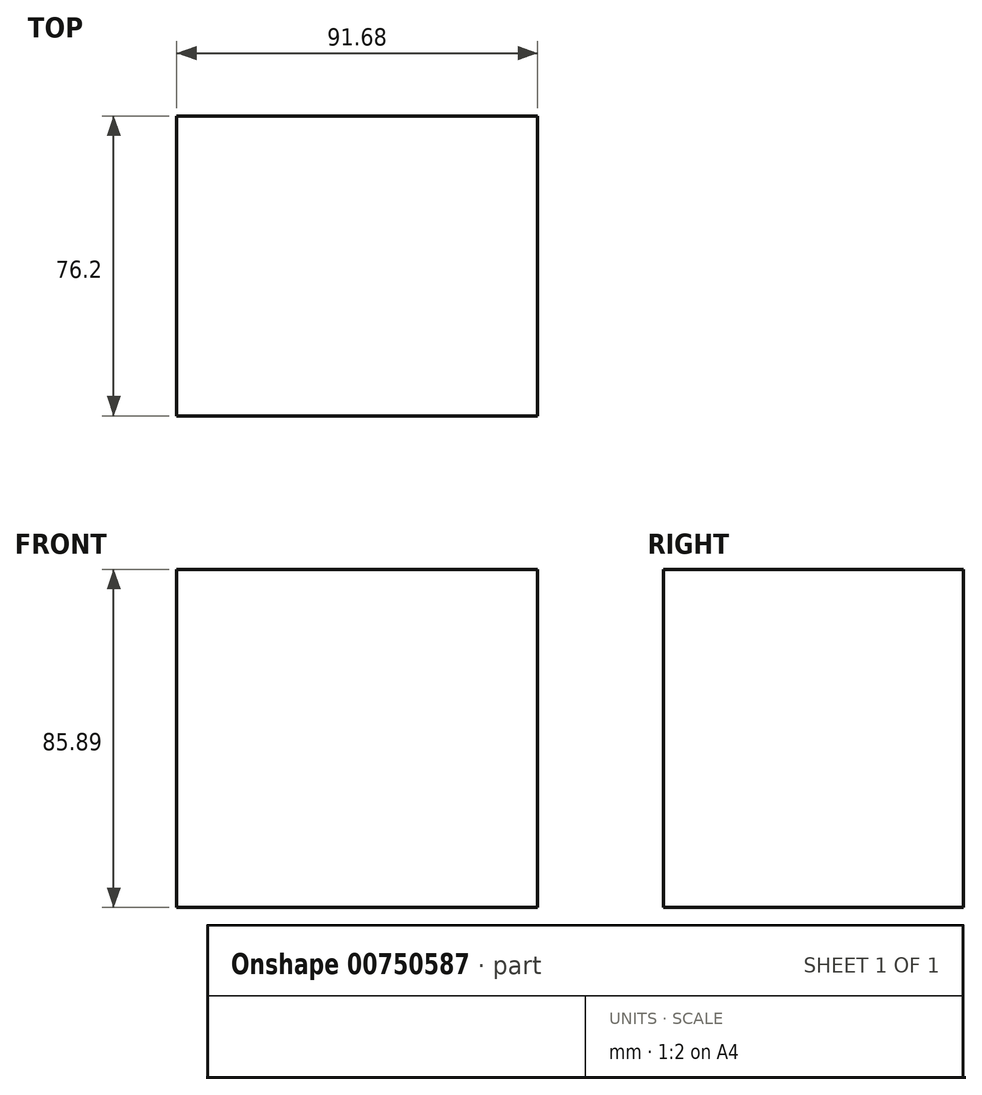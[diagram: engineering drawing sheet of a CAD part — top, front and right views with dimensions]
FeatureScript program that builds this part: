
annotation { "Feature Type Name" : "Feature", "Feature Type Description" : "" }
export const myFeature = defineFeature(function(context is Context, id is Id, definition is map)
    precondition{}
    {
        {
            var Q0;
            Q0=qCreatedBy(makeId("Front.planeOp"),FACE);
            var sketch = newSketch(context, id + "F0", { "sketchPlane" : qUnion([Q0])});
            skLineSegment(sketch, "E0.bottom", {"start": v(-50.04, -39.77) * mm, "end": v(41.64, -39.77) * mm});
            skLineSegment(sketch, "E0.top", {"start": v(-50.04, 46.12) * mm, "end": v(41.64, 46.12) * mm});
            skLineSegment(sketch, "E0.left", {"start": v(-50.04, -39.77) * mm, "end": v(-50.04, 46.12) * mm});
            skLineSegment(sketch, "E0.right", {"start": v(41.64, -39.77) * mm, "end": v(41.64, 46.12) * mm});
            skSolve(sketch);
        }
        {
            var Q0;
            Q0=makeQuery(id+"F0.imprint","IMPRINT",FACE,{"disambiguationData":[TD([[makeQuery(id+"F0.imprint","IMPRINT",EDGE,{"derivedFrom":sQuery(id+"F0.wireOp",EDGE,"E0.bottom")}),1.0]])]});
            extrude(context, id + "F1", {"entities" : qUnion([Q0]), "depth" : 76.2 * mm, "offsetDistance" : 25.4 * mm});
        }
    });
